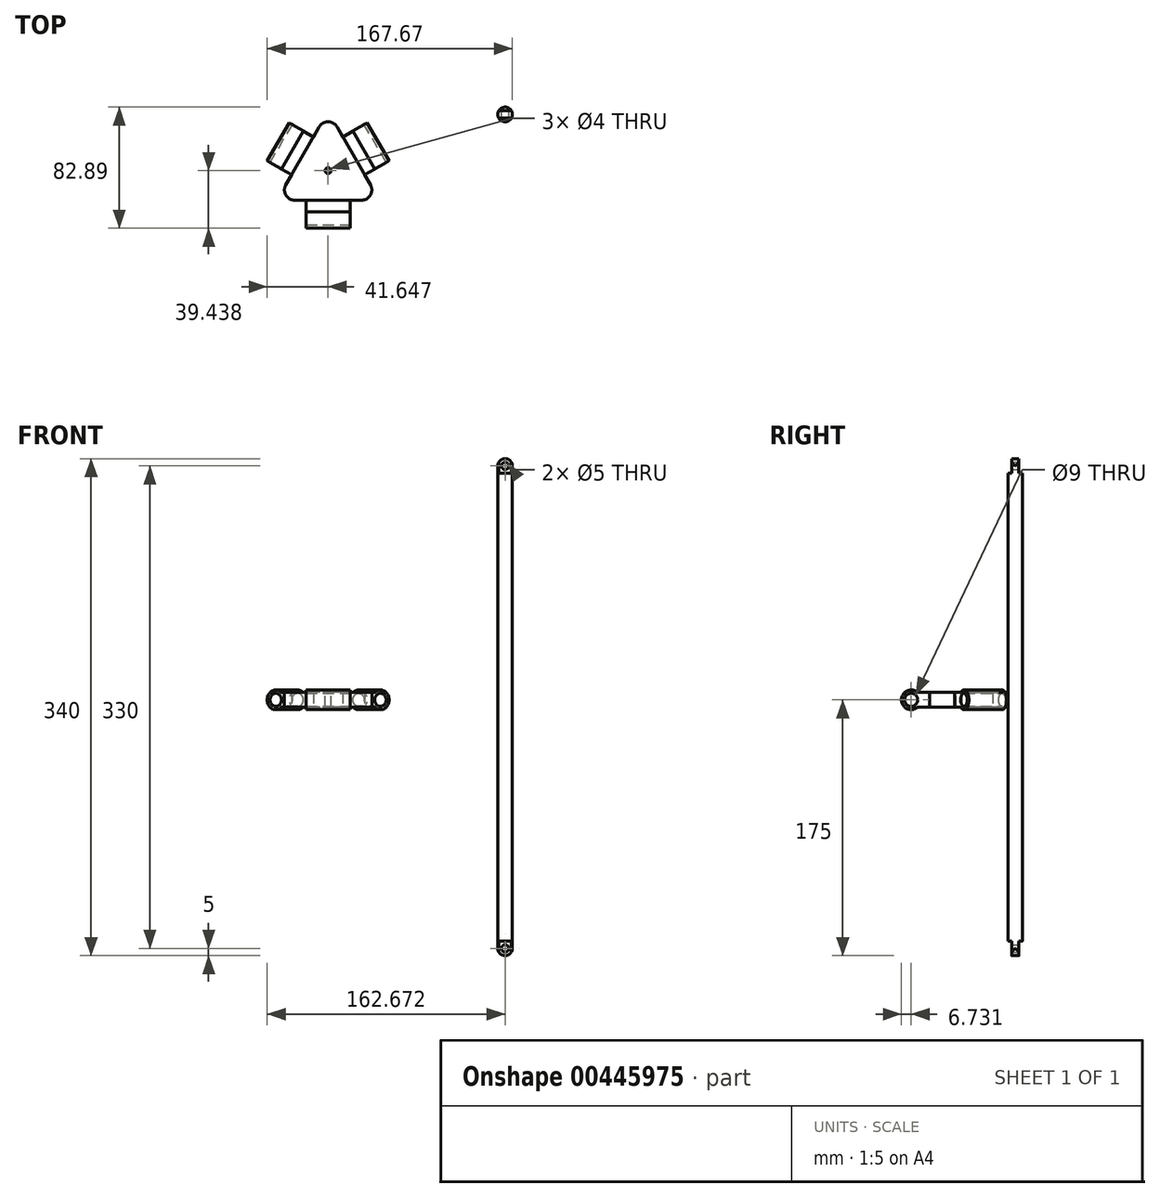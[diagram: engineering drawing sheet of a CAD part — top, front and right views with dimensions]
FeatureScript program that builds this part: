
annotation { "Feature Type Name" : "Feature", "Feature Type Description" : "" }
export const myFeature = defineFeature(function(context is Context, id is Id, definition is map)
    precondition{}
    {
        {
            var Q0;
            Q0=qCreatedBy(makeId("Top.planeOp"),FACE);
            var sketch = newSketch(context, id + "F0", { "sketchPlane" : qUnion([Q0])});
            skLineSegment(sketch, "E0.bottom", {"start": v(30, 15) * mm, "end": v(-30, 15) * mm});
            skLineSegment(sketch, "E0.top", {"start": v(30, -15) * mm, "end": v(-30, -15) * mm});
            skPoint(sketch, "E0.middle", {"position": v(0, 0) * mm});
            skArc(sketch, "E1", {"start": v(30, 15) * mm, "mid": v(45, 0) * mm, "end": v(30, -15) * mm});
            skArc(sketch, "E2", {"start": v(-30, 15) * mm, "mid": v(-45, 0) * mm, "end": v(-30, -15) * mm});
            skCircle(sketch, "E3", {"center": v(-30, 0) * mm, "radius": 10 * mm});
            skCircle(sketch, "E4", {"center": v(30, 0) * mm, "radius": 10 * mm});
            skSolve(sketch);
        }
        {
            var Q0;
            Q0 = qSketchRegion(id + "F0", true);
            extrude(context, id + "F1", {"entities" : qUnion([Q0]), "depth" : 30 * mm});
        }
        {
            var Q0;
            Q0=makeQuery(id+"F1.opExtrude","SWEPT_FACE",FACE,{"disambiguationData":[OSD([sQuery(id+"F0.wireOp",EDGE,"E0.bottom")])]});
            var sketch = newSketch(context, id + "F2", { "sketchPlane" : qUnion([Q0])});
            skLineSegment(sketch, "E5.bottom", {"start": v(-15, 22.5) * mm, "end": v(15, 22.5) * mm});
            skLineSegment(sketch, "E5.top", {"start": v(-15, 7.5) * mm, "end": v(15, 7.5) * mm});
            skLineSegment(sketch, "E5.left", {"start": v(-15, 22.5) * mm, "end": v(-15, 7.5) * mm});
            skLineSegment(sketch, "E5.right", {"start": v(15, 22.5) * mm, "end": v(15, 7.5) * mm});
            skSolve(sketch);
        }
        {
            var Q0;
            Q0 = qSketchRegion(id + "F2", true);
            extrude(context, id + "F3", {"entities" : qUnion([Q0]), "operationType" : NewBodyOperationType.ADD, "depth" : 10 * mm});
        }
        {
            var Q0;
            Q0=makeQuery(id+"F3.opExtrude","SWEPT_FACE",FACE,{"disambiguationData":[OSD([sQuery(id+"F2.wireOp",EDGE,"E5.right")])]});
            var sketch = newSketch(context, id + "F4", { "sketchPlane" : qUnion([Q0])});
            skCircle(sketch, "E6", {"center": v(-30, 15) * mm, "radius": 9 * mm});
            skPoint(sketch, "E6.centerSnap0", {"position": v(-25, 15) * mm});
            skCircle(sketch, "E7", {"center": v(-30, 15) * mm, "radius": 4.5 * mm});
            skSolve(sketch);
        }
        {
            var Q0;
            Q0 = qSketchRegion(id + "F4", true);
            var Q1;
            Q1=makeQuery(id+"F3.opExtrude","SWEPT_FACE",FACE,{"disambiguationData":[OSD([sQuery(id+"F2.wireOp",EDGE,"E5.left")])]});
            extrude(context, id + "F5", {"entities" : qUnion([Q0]), "operationType" : NewBodyOperationType.ADD, "endBound" : BoundingType.UP_TO_SURFACE, "oppositeDirection" : true, "endBoundEntityFace" : qUnion([Q1]), "depth" : 25 * mm});
        }
        {
            var Q0;
            Q0=qCreatedBy(makeId("Right.planeOp"),FACE);
            var sketch = newSketch(context, id + "F6", { "sketchPlane" : qUnion([Q0])});
            skCircle(sketch, "E8", {"center": v(44.58, 50.47) * mm, "radius": 4.5 * mm});
            skSolve(sketch);
        }
        {
            var Q0;
            Q0 = qSketchRegion(id + "F6", true);
            extrude(context, id + "F7", {"entities" : qUnion([Q0]), "oppositeDirection" : true, "depth" : 15 * mm});
        }
        {
            var Q0;
            Q0=makeQuery(id+"F7.opExtrude","CAP_FACE",FACE,{"disambiguationData":[OSD([sQuery(id+"F6.wireOp",EDGE,"E8")])],"isStart":false});
            var sketch = newSketch(context, id + "F8", { "sketchPlane" : qUnion([Q0])});
            skLineSegment(sketch, "E9.bottom", {"start": v(-41.58, 51.97) * mm, "end": v(-47.58, 51.97) * mm});
            skLineSegment(sketch, "E9.top", {"start": v(-41.58, 48.97) * mm, "end": v(-47.58, 48.97) * mm});
            skLineSegment(sketch, "E9.left", {"start": v(-41.58, 51.97) * mm, "end": v(-41.58, 48.97) * mm});
            skLineSegment(sketch, "E9.right", {"start": v(-47.58, 51.97) * mm, "end": v(-47.58, 48.97) * mm});
            skPoint(sketch, "E9.middle", {"position": v(-44.58, 50.47) * mm});
            skSolve(sketch);
        }
        {
            var Q0;
            Q0 = qSketchRegion(id + "F8", true);
            extrude(context, id + "F9", {"entities" : qUnion([Q0]), "operationType" : NewBodyOperationType.ADD, "depth" : 10 * mm});
        }
        {
            var Q0;
            Q0=makeQuery(id+"F9.opExtrude","SWEPT_FACE",FACE,{"disambiguationData":[OSD([sQuery(id+"F8.wireOp",EDGE,"E9.right")])]});
            var sketch = newSketch(context, id + "F10", { "sketchPlane" : qUnion([Q0])});
            skCircle(sketch, "E10", {"center": v(27, 50.47) * mm, "radius": 3 * mm});
            skPoint(sketch, "E10.centerSnap0", {"position": v(25, 50.47) * mm});
            skCircle(sketch, "E11", {"center": v(27, 50.47) * mm, "radius": 1.75 * mm});
            skSolve(sketch);
        }
        {
            var Q0;
            Q0 = qSketchRegion(id + "F10", true);
            var Q1;
            Q1=makeQuery(id+"F9.opExtrude","SWEPT_FACE",FACE,{"disambiguationData":[OSD([sQuery(id+"F8.wireOp",EDGE,"E9.left")])]});
            extrude(context, id + "F11", {"entities" : qUnion([Q0]), "operationType" : NewBodyOperationType.ADD, "endBound" : BoundingType.UP_TO_SURFACE, "oppositeDirection" : true, "endBoundEntityFace" : qUnion([Q1]), "depth" : 25 * mm});
        }
        {
            var Q0;
            Q0=makeQuery(id+"F7.opExtrude","SWEPT_BODY",BODY,{"disambiguationData":[OSD([sQuery(id+"F6.wireOp",EDGE,"E8")])]});
            var Q1;
            Q1=qCreatedBy(makeId("Right.planeOp"),FACE);
            mirror(context, id + "F12", {"operationType" : NewBodyOperationType.ADD, "entities" : qUnion([Q0]), "mirrorPlane" : qUnion([Q1])});
        }
        {
            var Q0;
            Q0=qCreatedBy(makeId("Top.planeOp"),FACE);
            var sketch = newSketch(context, id + "F13", { "sketchPlane" : qUnion([Q0])});
            skCircle(sketch, "E12", {"center": v(61.6, 0) * mm, "radius": 5 * mm});
            skSolve(sketch);
        }
        {
            var Q0;
            Q0 = qSketchRegion(id + "F13", true);
            extrude(context, id + "F14", {"entities" : qUnion([Q0]), "depth" : 160 * mm});
        }
        {
            var Q0;
            Q0=makeQuery(id+"F14.opExtrude","CAP_FACE",FACE,{"disambiguationData":[OSD([sQuery(id+"F13.wireOp",EDGE,"E12")])],"isStart":false});
            var sketch = newSketch(context, id + "F15", { "sketchPlane" : qUnion([Q0])});
            skPoint(sketch, "E13", {"position": v(66.6, 0) * mm});
            skPoint(sketch, "E14", {"position": v(56.6, 0) * mm});
            skSolve(sketch);
        }
        {
            var Q0;
            Q0=qCreatedBy(makeId("Front.planeOp"),FACE);
            var sketch = newSketch(context, id + "F16", { "sketchPlane" : qUnion([Q0])});
            skLineSegment(sketch, "E15", {"start": v(66.6, 160) * mm, "end": v(56.6, 160) * mm});
            skLineSegment(sketch, "E16", {"start": v(56.6, 160) * mm, "end": v(56.6, 165) * mm});
            skLineSegment(sketch, "E17", {"start": v(66.6, 165) * mm, "end": v(66.6, 160) * mm});
            skArc(sketch, "E18", {"start": v(66.6, 165) * mm, "mid": v(61.6, 170) * mm, "end": v(56.6, 165) * mm});
            skCircle(sketch, "E19", {"center": v(61.6, 165) * mm, "radius": 2.5 * mm});
            skSolve(sketch);
        }
        {
            var Q0;
            Q0 = qSketchRegion(id + "F16", true);
            extrude(context, id + "F17", {"entities" : qUnion([Q0]), "operationType" : NewBodyOperationType.ADD, "endBound" : BoundingType.SYMMETRIC, "depth" : 5 * mm});
        }
        {
            var Q0;
            Q0=makeQuery(id+"F15.imprint","IMPRINT",FACE,{"disambiguationData":[TD([[makeQuery(id+"F15.imprint","IMPRINT",EDGE,{"derivedFrom":makeQuery(id+"F14.opExtrude","CAP_EDGE",EDGE,{"disambiguationData":[OSD([sQuery(id+"F13.wireOp",EDGE,"E12")])],"isStart":false})}),1.0]])]});
            extrude(context, id + "F18", {"entities" : qUnion([Q0]), "operationType" : NewBodyOperationType.INTERSECT, "endBound" : BoundingType.SYMMETRIC, "depth" : 400 * mm});
        }
        {
            var Q0;
            Q0=makeQuery(id+"F14.opExtrude","SWEPT_BODY",BODY,{"disambiguationData":[OSD([sQuery(id+"F13.wireOp",EDGE,"E12")])]});
            var Q1;
            Q1=qCreatedBy(makeId("Top.planeOp"),FACE);
            mirror(context, id + "F19", {"operationType" : NewBodyOperationType.ADD, "entities" : qUnion([Q0]), "mirrorPlane" : qUnion([Q1])});
        }
        {
            var Q0;
            Q0=qCreatedBy(makeId("Top.planeOp"),FACE);
            var sketch = newSketch(context, id + "F20", { "sketchPlane" : qUnion([Q0])});
            skLineSegment(sketch, "E20", {"start": v(-65.5, -8.54) * mm, "end": v(-88.37, -48.16) * mm});
            skLineSegment(sketch, "E21", {"start": v(-82.3, -58.66) * mm, "end": v(-36.56, -58.66) * mm});
            skLineSegment(sketch, "E22", {"start": v(-30.5, -48.16) * mm, "end": v(-53.37, -8.54) * mm});
            skPoint(sketch, "E23.visualSharp", {"position": v(-59.43, 1.96) * mm});
            skArc(sketch, "E23.filletArc", {"start": v(-53.37, -8.54) * mm, "mid": v(-59.43, -5.04) * mm, "end": v(-65.5, -8.54) * mm});
            skPoint(sketch, "E24.visualSharp", {"position": v(-94.43, -58.66) * mm});
            skArc(sketch, "E24.filletArc", {"start": v(-88.37, -48.16) * mm, "mid": v(-88.37, -55.16) * mm, "end": v(-82.3, -58.66) * mm});
            skPoint(sketch, "E25.visualSharp", {"position": v(-24.43, -58.66) * mm});
            skArc(sketch, "E25.filletArc", {"start": v(-36.56, -58.66) * mm, "mid": v(-30.5, -55.16) * mm, "end": v(-30.5, -48.16) * mm});
            skSolve(sketch);
        }
        {
            var Q0;
            Q0 = qSketchRegion(id + "F20", true);
            extrude(context, id + "F21", {"entities" : qUnion([Q0]), "depth" : 10 * mm});
        }
        {
            var Q0;
            Q0=makeQuery(id+"F21.opExtrude","SWEPT_FACE",FACE,{"disambiguationData":[OSD([sQuery(id+"F20.wireOp",EDGE,"E20")])]});
            var sketch = newSketch(context, id + "F22", { "sketchPlane" : qUnion([Q0])});
            skLineSegment(sketch, "E26.bottom", {"start": v(48.02, 10) * mm, "end": v(78.02, 10) * mm});
            skLineSegment(sketch, "E26.top", {"start": v(48.02, 0) * mm, "end": v(78.02, 0) * mm});
            skLineSegment(sketch, "E26.left", {"start": v(48.02, 10) * mm, "end": v(48.02, 0) * mm});
            skLineSegment(sketch, "E26.right", {"start": v(78.02, 10) * mm, "end": v(78.02, 0) * mm});
            skSolve(sketch);
        }
        {
            var Q0;
            Q0 = qSketchRegion(id + "F22", true);
            extrude(context, id + "F23", {"entities" : qUnion([Q0]), "operationType" : NewBodyOperationType.ADD, "depth" : 8 * mm});
        }
        {
            var Q0;
            Q0=makeQuery(id+"F23.opExtrude","SWEPT_FACE",FACE,{"disambiguationData":[OSD([sQuery(id+"F22.wireOp",EDGE,"E26.right")])]});
            var sketch = newSketch(context, id + "F24", { "sketchPlane" : qUnion([Q0])});
            skCircle(sketch, "E27", {"center": v(-64.95, 5) * mm, "radius": 4.5 * mm});
            skPoint(sketch, "E27.centerSnap0", {"position": v(-60.45, 5) * mm});
            skCircle(sketch, "E28", {"center": v(-64.95, 5) * mm, "radius": 6.73 * mm});
            skSolve(sketch);
        }
        {
            var Q0;
            Q0 = qSketchRegion(id + "F24", true);
            var Q1;
            Q1=makeQuery(id+"F23.opExtrude","SWEPT_FACE",FACE,{"disambiguationData":[OSD([sQuery(id+"F22.wireOp",EDGE,"E26.left")])]});
            extrude(context, id + "F25", {"entities" : qUnion([Q0]), "operationType" : NewBodyOperationType.ADD, "endBound" : BoundingType.UP_TO_SURFACE, "oppositeDirection" : true, "endBoundEntityFace" : qUnion([Q1]), "depth" : 25 * mm});
        }
        {
            var Q0;
            Q0=makeQuery(id+"F23.boolean.opBoolean","MERGE",FACE,{"derivedFrom":[makeQuery(id+"F21.opExtrude","CAP_FACE",FACE,{"disambiguationData":[OSD([sQuery(id+"F20.wireOp",EDGE,"E20"),sQuery(id+"F20.wireOp",EDGE,"E21"),sQuery(id+"F20.wireOp",EDGE,"E22"),sQuery(id+"F20.wireOp",EDGE,"E23.filletArc"),sQuery(id+"F20.wireOp",EDGE,"E24.filletArc"),sQuery(id+"F20.wireOp",EDGE,"E25.filletArc")])],"isStart":false}),makeQuery(id+"F23.opExtrude","SWEPT_FACE",FACE,{"disambiguationData":[OSD([sQuery(id+"F22.wireOp",EDGE,"E26.bottom")])]})]});
            var sketch = newSketch(context, id + "F26", { "sketchPlane" : qUnion([Q0])});
            skLineSegment(sketch, "E29", {"start": v(-59.43, -58.66) * mm, "end": v(-59.43, -12.04) * mm, "construction": true});
            skLineSegment(sketch, "E30", {"start": v(-41.93, -28.35) * mm, "end": v(-82.3, -51.66) * mm, "construction": true});
            skPoint(sketch, "E31", {"position": v(-59.43, -38.45) * mm});
            skCircle(sketch, "E32", {"center": v(-59.43, -38.45) * mm, "radius": 2 * mm});
            skSolve(sketch);
        }
        {
            var Q0;
            Q0 = qSketchRegion(id + "F26", true);
            var Q1;
            Q1=makeQuery(id+"F23.boolean.opBoolean","MERGE",FACE,{"derivedFrom":[makeQuery(id+"F21.opExtrude","CAP_FACE",FACE,{"disambiguationData":[OSD([sQuery(id+"F20.wireOp",EDGE,"E20"),sQuery(id+"F20.wireOp",EDGE,"E21"),sQuery(id+"F20.wireOp",EDGE,"E22"),sQuery(id+"F20.wireOp",EDGE,"E23.filletArc"),sQuery(id+"F20.wireOp",EDGE,"E24.filletArc"),sQuery(id+"F20.wireOp",EDGE,"E25.filletArc")])],"isStart":true}),makeQuery(id+"F23.opExtrude","SWEPT_FACE",FACE,{"disambiguationData":[OSD([sQuery(id+"F22.wireOp",EDGE,"E26.top")])]})]});
            extrude(context, id + "F27", {"entities" : qUnion([Q0]), "operationType" : NewBodyOperationType.REMOVE, "endBound" : BoundingType.UP_TO_SURFACE, "oppositeDirection" : true, "endBoundEntityFace" : qUnion([Q1]), "depth" : 25 * mm});
        }
        {
            var Q0;
            Q0=makeQuery(id+"F21.opExtrude","SWEPT_BODY",BODY,{"disambiguationData":[OSD([sQuery(id+"F20.wireOp",EDGE,"E20"),sQuery(id+"F20.wireOp",EDGE,"E21"),sQuery(id+"F20.wireOp",EDGE,"E22"),sQuery(id+"F20.wireOp",EDGE,"E23.filletArc"),sQuery(id+"F20.wireOp",EDGE,"E24.filletArc"),sQuery(id+"F20.wireOp",EDGE,"E25.filletArc")])]});
            var Q1;
            Q1=makeQuery(id+"F27.boolean.opBoolean","COPY",FACE,{"derivedFrom":makeQuery(id+"F27.opExtrude","SWEPT_FACE",FACE,{"disambiguationData":[OSD([sQuery(id+"F26.wireOp",EDGE,"E32")])]})});
            circularPattern(context, id + "F28", {"operationType" : NewBodyOperationType.ADD, "entities" : qUnion([Q0]), "axis" : qUnion([Q1]), "angle" : 360 * degree, "instanceCount" : 3, "equalSpace" : true});
        }
    });
